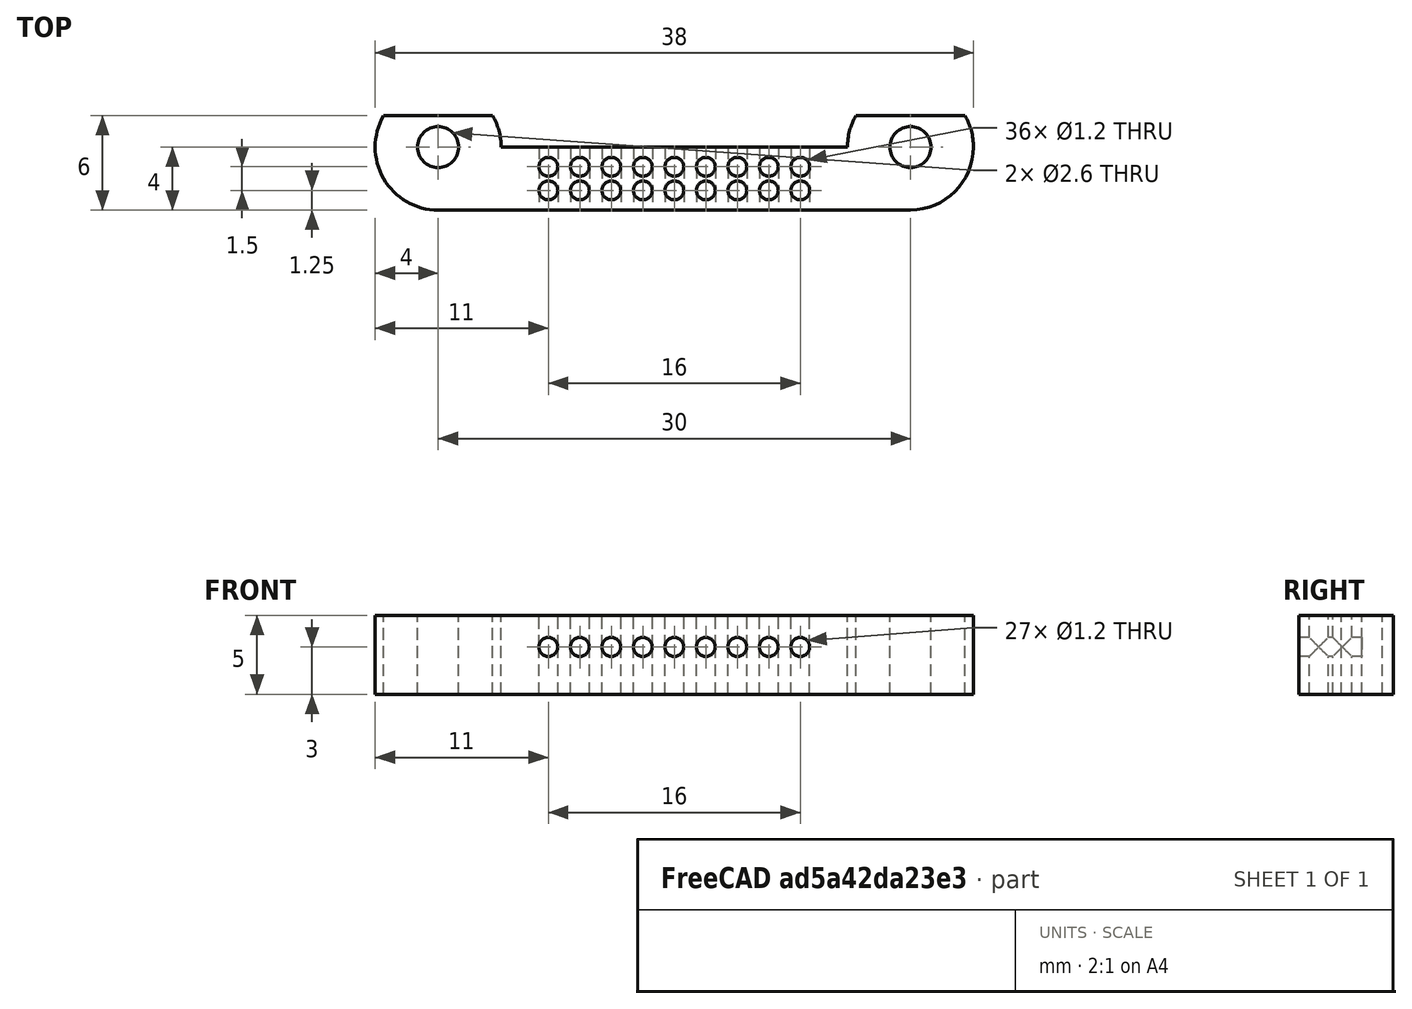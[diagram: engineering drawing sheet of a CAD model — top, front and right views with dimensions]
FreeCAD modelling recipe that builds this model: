
FCSTD DOCUMENT  (FreeCAD 0.19R19274 (Git))
Label: test_3
License: All rights reserved
LicenseURL: http://en.wikipedia.org/wiki/All_rights_reserved
objects: Part::Cylinder×31, Part::Cut×30, Part::Box×2, Part::MultiFuse×1, Mesh::Feature×1
note: 64 computed .brp shape members not serialized (recipe doc carries the construction recipe); baked Part::Feature solids carry a one-line shape summary decoded from their .brp

FEATURE [Part::Cylinder] Cylinder
  Angle = 360
  AttacherType = Attacher::AttachEngine3D
  Height = 5
  Placement = pos=(4,4,0) rot=(0,0,1;0rad)
  Radius = 4
FEATURE [Part::Cylinder] Cylinder001
  Angle = 360
  AttacherType = Attacher::AttachEngine3D
  Height = 5
  Placement = pos=(34,4,0) rot=(0,0,1;0rad)
  Radius = 4
FEATURE [Part::Box] Box  label="Cube"
  AttacherType = Attacher::AttachEngine3D
  Height = 5
  Length = 30
  Placement = pos=(4,0,0) rot=(0,0,1;0rad)
  Width = 4
FEATURE [Part::MultiFuse] Fusion
  Shapes = -> [Cylinder,Cylinder001,Box]
FEATURE [Part::Cylinder] Cylinder002
  Angle = 360
  AttacherType = Attacher::AttachEngine3D
  Height = 10
  Placement = pos=(4,4,-3) rot=(0,0,1;0rad)
  Radius = 1.3
FEATURE [Part::Cylinder] Cylinder003
  Angle = 360
  AttacherType = Attacher::AttachEngine3D
  Height = 10
  Placement = pos=(34,4,-1) rot=(0,0,1;0rad)
  Radius = 1.3
FEATURE [Part::Cylinder] Cylinder004 .. Cylinder012  x9 (patterned run collapsed; names and placements below)
  Angle = 360
  AttacherType = Attacher::AttachEngine3D
  Height = 10
  Radius = 0.6
  placements: 9 in arithmetic series — first pos=(11,2.75,-1) rot=(0,0,1;0rad), step (2,0,0), last pos=(27,2.75,-1) rot=(0,0,1;0rad)
FEATURE [Part::Cut] Cut
  Base = -> Fusion
  Tool = -> Cylinder002
FEATURE [Part::Cut] Cut001
  Base = -> Cut
  Tool = -> Cylinder012
FEATURE [Part::Cut] Cut002
  Base = -> Cut001
  Tool = -> Cylinder011
FEATURE [Part::Cut] Cut003
  Base = -> Cut002
  Tool = -> Cylinder010
FEATURE [Part::Cut] Cut004
  Base = -> Cut003
  Tool = -> Cylinder009
FEATURE [Part::Cut] Cut005
  Base = -> Cut004
  Tool = -> Cylinder008
FEATURE [Part::Cut] Cut006
  Base = -> Cut005
  Tool = -> Cylinder007
FEATURE [Part::Cut] Cut007
  Base = -> Cut006
  Tool = -> Cylinder006
FEATURE [Part::Cut] Cut008
  Base = -> Cut007
  Tool = -> Cylinder005
FEATURE [Part::Cut] Cut009
  Base = -> Cut008
  Tool = -> Cylinder004
FEATURE [Part::Cut] Cut010
  Base = -> Cut009
  Tool = -> Cylinder003
FEATURE [Part::Box] Box001  label="Cube001"
  AttacherType = Attacher::AttachEngine3D
  Height = 10
  Length = 40
  Placement = pos=(0,6,-1) rot=(0,0,1;0rad)
  Width = 10
FEATURE [Part::Cut] Cut011
  Base = -> Cut010
  Tool = -> Box001
FEATURE [Part::Cylinder] Cylinder013
  Angle = 360
  AttacherType = Attacher::AttachEngine3D
  Height = 10
  Placement = pos=(11,7,3) rot=(1,0,0;1.5708rad)
  Radius = 0.6
FEATURE [Part::Cylinder] Cylinder014
  Angle = 360
  AttacherType = Attacher::AttachEngine3D
  Height = 10
  Placement = pos=(13,7,3) rot=(1,0,0;1.5708rad)
  Radius = 0.6
FEATURE [Part::Cylinder] Cylinder015
  Angle = 360
  AttacherType = Attacher::AttachEngine3D
  Height = 10
  Placement = pos=(15,7,3) rot=(1,0,0;1.5708rad)
  Radius = 0.6
FEATURE [Part::Cylinder] Cylinder016
  Angle = 360
  AttacherType = Attacher::AttachEngine3D
  Height = 10
  Placement = pos=(17,7,3) rot=(1,0,0;1.5708rad)
  Radius = 0.6
FEATURE [Part::Cylinder] Cylinder017
  Angle = 360
  AttacherType = Attacher::AttachEngine3D
  Height = 10
  Placement = pos=(19,7,3) rot=(1,0,0;1.5708rad)
  Radius = 0.6
FEATURE [Part::Cylinder] Cylinder018
  Angle = 360
  AttacherType = Attacher::AttachEngine3D
  Height = 10
  Placement = pos=(21,7,3) rot=(1,0,0;1.5708rad)
  Radius = 0.6
FEATURE [Part::Cylinder] Cylinder019
  Angle = 360
  AttacherType = Attacher::AttachEngine3D
  Height = 10
  Placement = pos=(23,7,3) rot=(1,0,0;1.5708rad)
  Radius = 0.6
FEATURE [Part::Cylinder] Cylinder020
  Angle = 360
  AttacherType = Attacher::AttachEngine3D
  Height = 10
  Placement = pos=(25,7,3) rot=(1,0,0;1.5708rad)
  Radius = 0.6
FEATURE [Part::Cylinder] Cylinder021
  Angle = 360
  AttacherType = Attacher::AttachEngine3D
  Height = 10
  Placement = pos=(27,7,3) rot=(1,0,0;1.5708rad)
  Radius = 0.6
FEATURE [Part::Cylinder] Cylinder022
  Angle = 360
  AttacherType = Attacher::AttachEngine3D
  Height = 10
  Placement = pos=(11,1.25,-1) rot=(0,0,1;0rad)
  Radius = 0.6
FEATURE [Part::Cylinder] Cylinder023
  Angle = 360
  AttacherType = Attacher::AttachEngine3D
  Height = 10
  Placement = pos=(13,1.25,-1) rot=(0,0,1;0rad)
  Radius = 0.6
FEATURE [Part::Cylinder] Cylinder024
  Angle = 360
  AttacherType = Attacher::AttachEngine3D
  Height = 10
  Placement = pos=(15,1.25,-1) rot=(0,0,1;0rad)
  Radius = 0.6
FEATURE [Part::Cylinder] Cylinder025
  Angle = 360
  AttacherType = Attacher::AttachEngine3D
  Height = 10
  Placement = pos=(17,1.25,-1) rot=(0,0,1;0rad)
  Radius = 0.6
FEATURE [Part::Cylinder] Cylinder026
  Angle = 360
  AttacherType = Attacher::AttachEngine3D
  Height = 10
  Placement = pos=(19,1.25,-1) rot=(0,0,1;0rad)
  Radius = 0.6
FEATURE [Part::Cylinder] Cylinder027
  Angle = 360
  AttacherType = Attacher::AttachEngine3D
  Height = 10
  Placement = pos=(21,1.25,-1) rot=(0,0,1;0rad)
  Radius = 0.6
FEATURE [Part::Cylinder] Cylinder028
  Angle = 360
  AttacherType = Attacher::AttachEngine3D
  Height = 10
  Placement = pos=(23,1.25,-1) rot=(0,0,1;0rad)
  Radius = 0.6
FEATURE [Part::Cylinder] Cylinder029
  Angle = 360
  AttacherType = Attacher::AttachEngine3D
  Height = 10
  Placement = pos=(25,1.25,-1) rot=(0,0,1;0rad)
  Radius = 0.6
FEATURE [Part::Cylinder] Cylinder030
  Angle = 360
  AttacherType = Attacher::AttachEngine3D
  Height = 10
  Placement = pos=(27,1.25,-1) rot=(0,0,1;0rad)
  Radius = 0.6
FEATURE [Part::Cut] Cut012
  Base = -> Cut011
  Tool = -> Cylinder013
FEATURE [Part::Cut] Cut013
  Base = -> Cut012
  Tool = -> Cylinder030
FEATURE [Part::Cut] Cut014
  Base = -> Cut013
  Tool = -> Cylinder029
FEATURE [Part::Cut] Cut015
  Base = -> Cut014
  Tool = -> Cylinder028
FEATURE [Part::Cut] Cut016
  Base = -> Cut015
  Tool = -> Cylinder027
FEATURE [Part::Cut] Cut017
  Base = -> Cut016
  Tool = -> Cylinder026
FEATURE [Part::Cut] Cut018
  Base = -> Cut017
  Tool = -> Cylinder025
FEATURE [Part::Cut] Cut019
  Base = -> Cut018
  Tool = -> Cylinder024
FEATURE [Part::Cut] Cut020
  Base = -> Cut019
  Tool = -> Cylinder023
FEATURE [Part::Cut] Cut021
  Base = -> Cut020
  Tool = -> Cylinder022
FEATURE [Part::Cut] Cut022
  Base = -> Cut021
  Tool = -> Cylinder021
FEATURE [Part::Cut] Cut023
  Base = -> Cut022
  Tool = -> Cylinder020
FEATURE [Part::Cut] Cut024
  Base = -> Cut023
  Tool = -> Cylinder019
FEATURE [Part::Cut] Cut025
  Base = -> Cut024
  Tool = -> Cylinder018
FEATURE [Part::Cut] Cut026
  Base = -> Cut025
  Tool = -> Cylinder017
FEATURE [Part::Cut] Cut027
  Base = -> Cut026
  Tool = -> Cylinder016
FEATURE [Part::Cut] Cut028
  Base = -> Cut027
  Tool = -> Cylinder015
FEATURE [Part::Cut] Cut029
  Base = -> Cut028
  Tool = -> Cylinder014
FEATURE [Mesh::Feature] Mesh  label="Cut029 (Meshed)"
